# Revit family: Zumtobel VIVO L LED
name_source: partatom
category: Lighting Fixtures
revit_build: Autodesk Revit 2016 (Build: 20150220_1215(x64)
units: mm (PartAtom-declared; Revit-internal decimal feet)

## family parameters
Cut with Voids When Loaded = No
Host = Face
Light Source = No
OmniClass Number = 23.80.70.11
OmniClass Title = Luminaries for Internal Lighting
Part Type = Normal
Room Calculation Point = No
Round Connector Dimension = Use Diameter
Shared = No

## types (8) — shared parameters
Assembly Code = D5020200
Description = LED Spotlight - Large
Emit Shape Visible in Rendering = Yes
Lamp = LED
Length = 130 mm  [stored 0.426509 ft]
Manufacturer = Zumtobel Lighting
URL = http://www.zumtobel.com
Voltage = 230 V
zero-valued in all types: Default Elevation

## per-type parameters (varying)
| type | 3CV Track | Apparent Load | Body Type | Height | Model | Tecton Track | Width |
| VIVO L LED6000 3CV | Yes | 59 VA | Zumtobel VIVO L Body : VIVO L LED6000 3CV | 250 mm  [stored 0.82021 ft] | 60714032 | No | 260 mm  [stored 0.853018 ft] |
| VIVO L LED6000 TEC | No | 61 VA | Zumtobel VIVO L Body : VIVO L LED6000 TEC | 232 mm  [stored 0.761155 ft] | 60714056 | Yes | 498 mm  [stored 1.63386 ft] |
| VIVO L LED5000 3CV | Yes | 59 VA | Zumtobel VIVO L Body : VIVO L LED5000 3CV | 250 mm  [stored 0.82021 ft] | 60714068 | No | 260 mm  [stored 0.853018 ft] |
| VIVO L LED5000 TEC | No | 61 VA | Zumtobel VIVO L Body : VIVO L LED5000 TEC | 232 mm  [stored 0.761155 ft] | 60714092 | Yes | 498 mm  [stored 1.63386 ft] |
| VIVO L LED5800 3CV | Yes | 59 VA | Zumtobel VIVO L Body : VIVO L LED5800 3CV | 250 mm  [stored 0.82021 ft] | 60714835 | No | 260 mm  [stored 0.853018 ft] |
| VIVO L LED5800 TEC | No | 59 VA | Zumtobel VIVO L Body : VIVO L LED5800 TEC | 232 mm  [stored 0.761155 ft] | 60714851 | Yes | 498 mm  [stored 1.63386 ft] |
| VIVO L LED4800 3CV | Yes | 59 VA | Zumtobel VIVO L Body : VIVO L LED4800 3CV | 250 mm  [stored 0.82021 ft] | 60714859 | No | 260 mm  [stored 0.853018 ft] |
| VIVO L LED4800 TEC | No | 59 VA | Zumtobel VIVO L Body : VIVO L LED4800 TEC | 250 mm  [stored 0.82021 ft] | 60714875 | Yes | 260 mm  [stored 0.853018 ft] |

note: [stored X ft] marks values corroborated as IEEE doubles in the binary element streams (Revit-internal decimal feet)

## geometry (parser evidence)
native form markers: Sweep x6
no freeform markers — native parametric forms only
